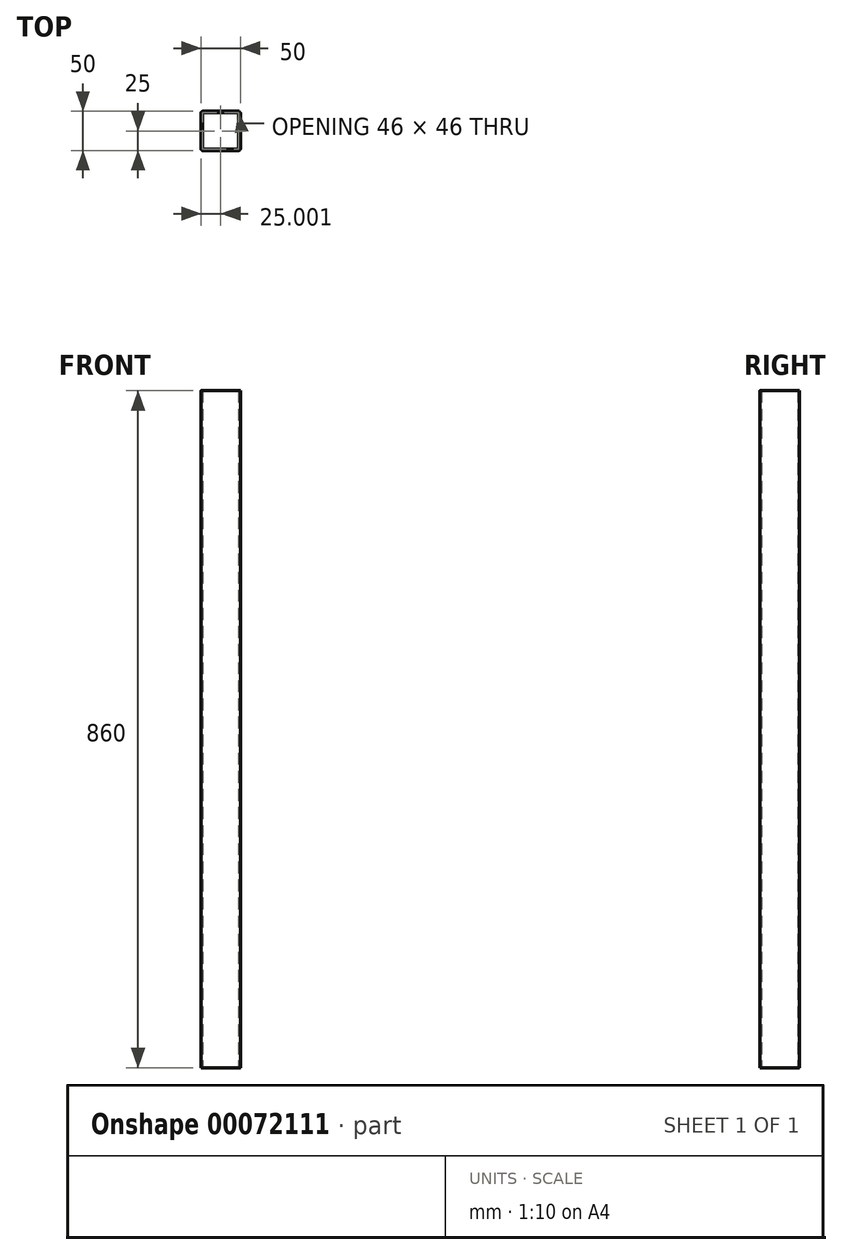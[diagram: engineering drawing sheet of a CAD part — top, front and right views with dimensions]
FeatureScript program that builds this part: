
annotation { "Feature Type Name" : "Feature", "Feature Type Description" : "" }
export const myFeature = defineFeature(function(context is Context, id is Id, definition is map)
    precondition{}
    {
        {
            var Q0;
            Q0=qCreatedBy(makeId("Top.planeOp"),FACE);
            var sketch = newSketch(context, id + "F0", { "sketchPlane" : qUnion([Q0])});
            skLineSegment(sketch, "E0.bottom", {"start": v(-54.16, 61.71) * mm, "end": v(-4.16, 61.71) * mm});
            skLineSegment(sketch, "E0.top", {"start": v(-54.16, 11.71) * mm, "end": v(-4.16, 11.71) * mm});
            skLineSegment(sketch, "E0.left", {"start": v(-54.16, 61.71) * mm, "end": v(-54.16, 11.71) * mm});
            skLineSegment(sketch, "E0.right", {"start": v(-4.16, 61.71) * mm, "end": v(-4.16, 11.71) * mm});
            skLineSegment(sketch, "E1.0", {"start": v(-52.16, 59.71) * mm, "end": v(-6.16, 59.71) * mm});
            skLineSegment(sketch, "E1.1", {"start": v(-52.16, 59.71) * mm, "end": v(-52.16, 13.71) * mm});
            skLineSegment(sketch, "E1.2", {"start": v(-52.16, 13.71) * mm, "end": v(-6.16, 13.71) * mm});
            skLineSegment(sketch, "E1.3", {"start": v(-6.16, 59.71) * mm, "end": v(-6.16, 13.71) * mm});
            skSolve(sketch);
        }
        {
            var Q0;
            Q0=makeQuery(id+"F0.imprint","IMPRINT",FACE,{"disambiguationData":[TD([[makeQuery(id+"F0.imprint","IMPRINT",EDGE,{"derivedFrom":sQuery(id+"F0.wireOp",EDGE,"E0.bottom")}),-1.0]])]});
            extrude(context, id + "F1", {"entities" : qUnion([Q0]), "depth" : 860 * mm});
        }
        {
            var Q0;
            Q0=makeQuery(id+"F1.opExtrude","SWEPT_EDGE",EDGE,{"disambiguationData":[OSD([sQuery(id+"F0.wireOp",EDGE,"E0.bottom"),sQuery(id+"F0.wireOp",EDGE,"E0.right")])]});
            var Q1;
            Q1=makeQuery(id+"F1.opExtrude","SWEPT_EDGE",EDGE,{"disambiguationData":[OSD([sQuery(id+"F0.wireOp",EDGE,"E0.bottom"),sQuery(id+"F0.wireOp",EDGE,"E0.left")])]});
            var Q2;
            Q2=makeQuery(id+"F1.opExtrude","SWEPT_EDGE",EDGE,{"disambiguationData":[OSD([sQuery(id+"F0.wireOp",EDGE,"E0.top"),sQuery(id+"F0.wireOp",EDGE,"E0.right")])]});
            var Q3;
            Q3=makeQuery(id+"F1.opExtrude","SWEPT_EDGE",EDGE,{"disambiguationData":[OSD([sQuery(id+"F0.wireOp",EDGE,"E0.top"),sQuery(id+"F0.wireOp",EDGE,"E0.left")])]});
            fillet(context, id + "F2", {"entities" : qUnion([Q0, Q1, Q2, Q3]), "radius" : 2.5 * mm, "tangentPropagation" : true, "allowEdgeOverflow" : false});
        }
        {
            var Q0;
            Q0=makeQuery(id+"F1.opExtrude","SWEPT_EDGE",EDGE,{"disambiguationData":[OSD([sQuery(id+"F0.wireOp",EDGE,"E1.0"),sQuery(id+"F0.wireOp",EDGE,"E1.3")])]});
            var Q1;
            Q1=makeQuery(id+"F1.opExtrude","SWEPT_EDGE",EDGE,{"disambiguationData":[OSD([sQuery(id+"F0.wireOp",EDGE,"E1.0"),sQuery(id+"F0.wireOp",EDGE,"E1.1")])]});
            var Q2;
            Q2=makeQuery(id+"F1.opExtrude","SWEPT_EDGE",EDGE,{"disambiguationData":[OSD([sQuery(id+"F0.wireOp",EDGE,"E1.1"),sQuery(id+"F0.wireOp",EDGE,"E1.2")])]});
            var Q3;
            Q3=makeQuery(id+"F1.opExtrude","SWEPT_EDGE",EDGE,{"disambiguationData":[OSD([sQuery(id+"F0.wireOp",EDGE,"E1.2"),sQuery(id+"F0.wireOp",EDGE,"E1.3")])]});
            fillet(context, id + "F3", {"entities" : qUnion([Q0, Q1, Q2, Q3]), "radius" : 2.5 * mm, "tangentPropagation" : true, "allowEdgeOverflow" : false});
        }
        {
            var Q0;
            Q0=makeQuery(id+"F1.opExtrude","SWEPT_BODY",BODY,{"disambiguationData":[OSD([sQuery(id+"F0.wireOp",EDGE,"E0.bottom"),sQuery(id+"F0.wireOp",EDGE,"E0.top"),sQuery(id+"F0.wireOp",EDGE,"E0.left"),sQuery(id+"F0.wireOp",EDGE,"E0.right"),sQuery(id+"F0.wireOp",EDGE,"E1.0"),sQuery(id+"F0.wireOp",EDGE,"E1.1"),sQuery(id+"F0.wireOp",EDGE,"E1.2"),sQuery(id+"F0.wireOp",EDGE,"E1.3")])]});
            transform(context, id + "F4", {"entities" : qUnion([Q0]), "transformType" : TransformType.TRANSLATION_3D, "dx" : 0 * mm, "dy" : 0 * mm, "dz" : 0 * mm, "makeCopy" : true});
        }
        {
            var Q0;
            Q0=makeQuery(id+"F4.opPattern","COPY",BODY,{"derivedFrom":makeQuery(id+"F1.opExtrude","SWEPT_BODY",BODY,{"disambiguationData":[OSD([sQuery(id+"F0.wireOp",EDGE,"E0.bottom"),sQuery(id+"F0.wireOp",EDGE,"E0.top"),sQuery(id+"F0.wireOp",EDGE,"E0.left"),sQuery(id+"F0.wireOp",EDGE,"E0.right"),sQuery(id+"F0.wireOp",EDGE,"E1.0"),sQuery(id+"F0.wireOp",EDGE,"E1.1"),sQuery(id+"F0.wireOp",EDGE,"E1.2"),sQuery(id+"F0.wireOp",EDGE,"E1.3")])]}),"instanceName":"1"});
            deleteBodies(context, id + "F5", {"entities" : qUnion([Q0])});
        }
        {
            var Q0;
            Q0=makeQuery(id+"F1.opExtrude","SWEPT_BODY",BODY,{"disambiguationData":[OSD([sQuery(id+"F0.wireOp",EDGE,"E0.bottom"),sQuery(id+"F0.wireOp",EDGE,"E0.top"),sQuery(id+"F0.wireOp",EDGE,"E0.left"),sQuery(id+"F0.wireOp",EDGE,"E0.right"),sQuery(id+"F0.wireOp",EDGE,"E1.0"),sQuery(id+"F0.wireOp",EDGE,"E1.1"),sQuery(id+"F0.wireOp",EDGE,"E1.2"),sQuery(id+"F0.wireOp",EDGE,"E1.3")])]});
            transform(context, id + "F6", {"entities" : qUnion([Q0]), "transformType" : TransformType.TRANSLATION_3D, "dx" : 0 * mm, "dy" : 0 * mm, "dz" : 0 * mm, "makeCopy" : true});
        }
        {
            var Q0;
            Q0=makeQuery(id+"F6.opPattern","COPY",BODY,{"derivedFrom":makeQuery(id+"F1.opExtrude","SWEPT_BODY",BODY,{"disambiguationData":[OSD([sQuery(id+"F0.wireOp",EDGE,"E0.bottom"),sQuery(id+"F0.wireOp",EDGE,"E0.top"),sQuery(id+"F0.wireOp",EDGE,"E0.left"),sQuery(id+"F0.wireOp",EDGE,"E0.right"),sQuery(id+"F0.wireOp",EDGE,"E1.0"),sQuery(id+"F0.wireOp",EDGE,"E1.1"),sQuery(id+"F0.wireOp",EDGE,"E1.2"),sQuery(id+"F0.wireOp",EDGE,"E1.3")])]}),"instanceName":"1"});
            deleteBodies(context, id + "F7", {"entities" : qUnion([Q0])});
        }
    });
